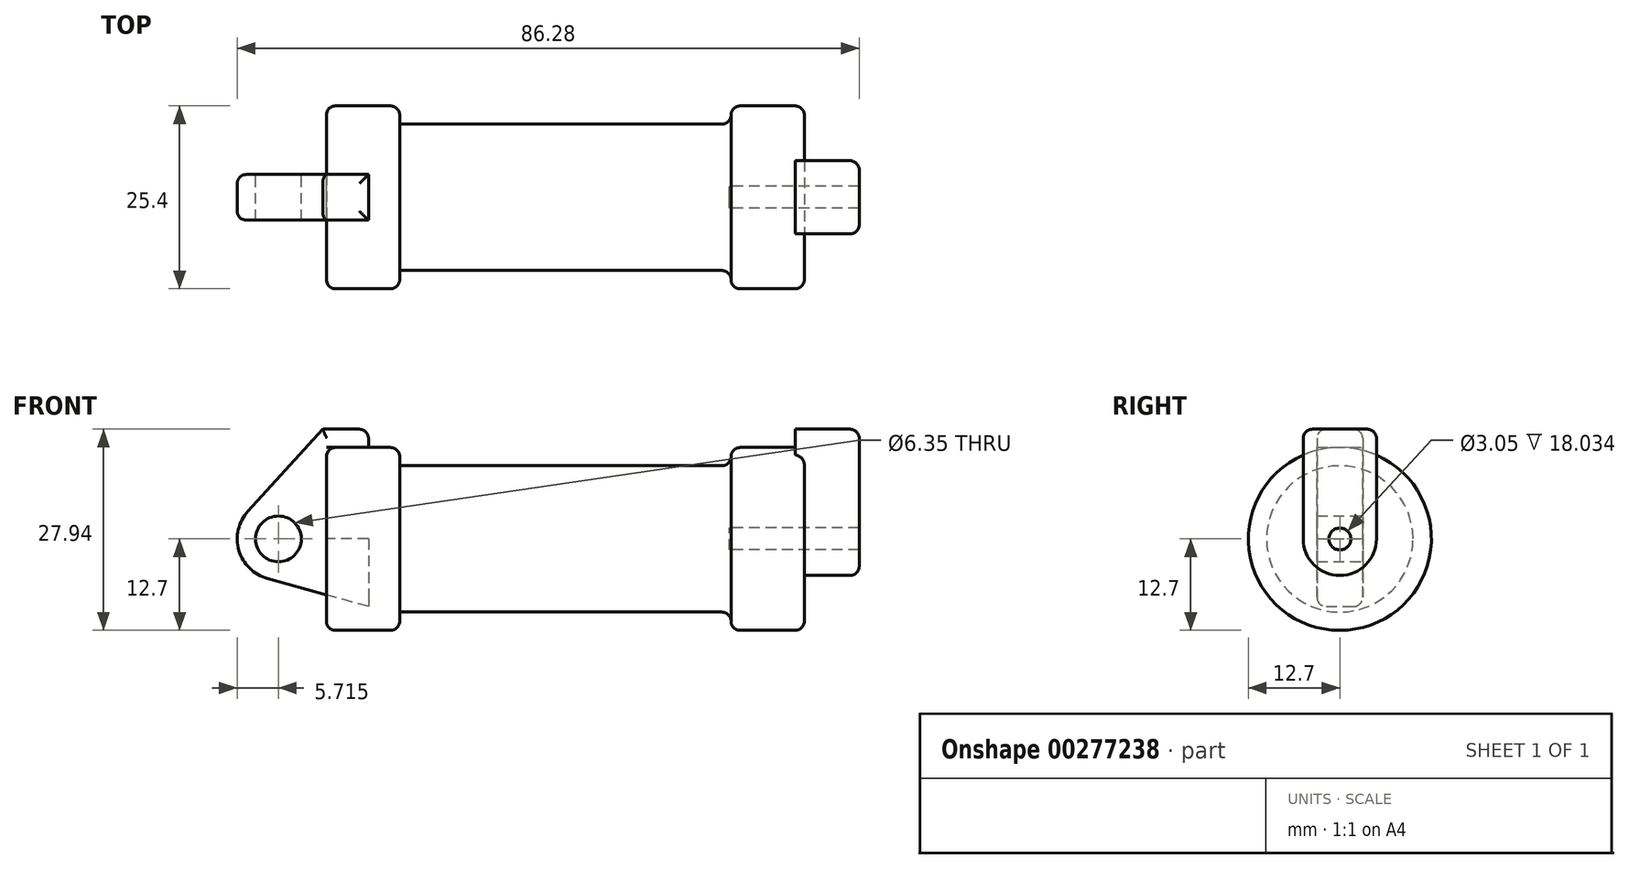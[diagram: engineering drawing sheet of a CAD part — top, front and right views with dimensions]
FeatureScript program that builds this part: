
annotation { "Feature Type Name" : "Feature", "Feature Type Description" : "" }
export const myFeature = defineFeature(function(context is Context, id is Id, definition is map)
    precondition{}
    {
        {
            var Q0;
            Q0=qCreatedBy(makeId("Front.planeOp"),FACE);
            var sketch = newSketch(context, id + "F0", { "sketchPlane" : qUnion([Q0])});
            skLineSegment(sketch, "E0", {"start": v(0, 0) * mm, "end": v(0, 12.7) * mm});
            skLineSegment(sketch, "E1", {"start": v(0, 12.7) * mm, "end": v(10.16, 12.7) * mm});
            skLineSegment(sketch, "E2", {"start": v(10.16, 12.7) * mm, "end": v(10.16, 10.16) * mm});
            skLineSegment(sketch, "E3", {"start": v(10.16, 10.16) * mm, "end": v(56.13, 10.16) * mm});
            skLineSegment(sketch, "E4", {"start": v(56.13, 10.16) * mm, "end": v(56.13, 12.7) * mm});
            skLineSegment(sketch, "E5", {"start": v(56.13, 12.7) * mm, "end": v(66.3, 12.7) * mm});
            skLineSegment(sketch, "E6", {"start": v(66.3, 12.7) * mm, "end": v(66.3, 0) * mm});
            skLineSegment(sketch, "E7", {"start": v(66.3, 0) * mm, "end": v(0, 0) * mm});
            skLineSegment(sketch, "E8", {"start": v(5.84, 15.24) * mm, "end": v(-0.5, 15.24) * mm});
            skLineSegment(sketch, "E9", {"start": v(-0.5, 15.24) * mm, "end": v(-10.88, 3.85) * mm});
            skLineSegment(sketch, "E10", {"start": v(0, 0) * mm, "end": v(-6.65, 0) * mm});
            skCircle(sketch, "E11", {"center": v(-6.65, 0) * mm, "radius": 5.72 * mm});
            skCircle(sketch, "E12", {"center": v(-6.65, 0) * mm, "radius": 3.18 * mm});
            skLineSegment(sketch, "E13", {"start": v(5.84, 15.24) * mm, "end": v(5.84, -9.4) * mm});
            skLineSegment(sketch, "E14", {"start": v(5.84, -9.4) * mm, "end": v(-8.18, -5.5) * mm});
            skSolve(sketch);
        }
        {
            var Q0;
            {var subQ0=sQuery(id+"F0.wireOp",EDGE,"E2");Q0=makeQuery(id+"F0.imprint","IMPRINT",FACE,{"disambiguationData":[TD([[makeQuery(id+"F0.imprint","IMPRINT",EDGE,{"derivedFrom":subQ0}),-1.0]])]});}
            var Q1;
            {var subQ0=sQuery(id+"F0.wireOp",EDGE,"E0");Q1=makeQuery(id+"F0.imprint","IMPRINT",FACE,{"disambiguationData":[TD([[makeQuery(id+"F0.imprint","IMPRINT",EDGE,{"derivedFrom":subQ0}),-1.0]])]});}
            var Q2;
            Q2=sQuery(id+"F0.wireOp",EDGE,"E7");
            revolve(context, id + "F1", {"entities" : qUnion([Q0, Q1]), "axis" : qUnion([Q2]), "revolveType" : RevolveType.FULL});
        }
        {
            var Q0;
            {var subQ4=sQuery(id+"F0.wireOp",EDGE,"E12");Q0=makeQuery(id+"F0.imprint","IMPRINT",FACE,{"disambiguationData":[TD([[makeQuery(id+"F0.imprint","IMPRINT",EDGE,{"derivedFrom":subQ4}),-1.0]])]});}
            var Q1;
            {var subQ0=sQuery(id+"F0.wireOp",EDGE,"E14");Q1=makeQuery(id+"F0.imprint","IMPRINT",FACE,{"disambiguationData":[TD([[makeQuery(id+"F0.imprint","IMPRINT",EDGE,{"derivedFrom":subQ0}),-1.0]])]});}
            var Q2;
            {var subQ3=sQuery(id+"F0.wireOp",EDGE,"E0");Q2=makeQuery(id+"F0.imprint","IMPRINT",FACE,{"disambiguationData":[TD([[makeQuery(id+"F0.imprint","IMPRINT",EDGE,{"derivedFrom":subQ3}),1.0]])]});}
            extrude(context, id + "F2", {"entities" : qUnion([Q0, Q1, Q2]), "depth" : 3.17 * mm, "hasSecondDirection" : true, "secondDirectionOppositeDirection" : true, "secondDirectionDepth" : 3.17 * mm});
        }
        {
            var Q0;
            Q0=makeQuery(id+"F1.opRevolve","SWEPT_FACE",FACE,{"disambiguationData":[OSD([sQuery(id+"F0.wireOp",EDGE,"E6")])]});
            var sketch = newSketch(context, id + "F3", { "sketchPlane" : qUnion([Q0])});
            skCircle(sketch, "E15", {"center": v(0, 0) * mm, "radius": 1.52 * mm});
            skCircle(sketch, "E16", {"center": v(0, 0) * mm, "radius": 5.08 * mm});
            skLineSegment(sketch, "E17", {"start": v(-5.08, 0) * mm, "end": v(-5.08, 15.24) * mm});
            skLineSegment(sketch, "E18", {"start": v(5.08, 0) * mm, "end": v(5.08, 15.24) * mm});
            skLineSegment(sketch, "E19", {"start": v(-5.08, 15.24) * mm, "end": v(5.08, 15.24) * mm});
            skSolve(sketch);
        }
        {
            var Q0;
            Q0=makeQuery(id+"F3.imprint","IMPRINT",FACE,{"disambiguationData":[TD([[makeQuery(id+"F3.imprint","IMPRINT",EDGE,{"derivedFrom":sQuery(id+"F3.wireOp",EDGE,"E15")}),-1.0]])]});
            var Q1;
            {var subQ0=sQuery(id+"F3.wireOp",EDGE,"E17");var subQ1=sQuery(id+"F3.wireOp",EDGE,"E16");var subQ2=makeQuery(id+"F3.imprint","INTERSECT",VERTEX,{"derivedFrom":[subQ1,subQ0]});Q1=makeQuery(id+"F3.imprint","IMPRINT",FACE,{"disambiguationData":[TD([[makeQuery(id+"F3.imprint","IMPRINT",EDGE,{"disambiguationData":[TD([[subQ2,1.0]])],"derivedFrom":subQ1}),-1.0]])]});}
            var Q2;
            {var subQ0=sQuery(id+"F3.wireOp",EDGE,"E19");Q2=makeQuery(id+"F3.imprint","IMPRINT",FACE,{"disambiguationData":[TD([[makeQuery(id+"F3.imprint","IMPRINT",EDGE,{"derivedFrom":subQ0}),-1.0]])]});}
            extrude(context, id + "F4", {"entities" : qUnion([Q0, Q1, Q2]), "operationType" : NewBodyOperationType.ADD, "depth" : 7.62 * mm});
        }
        {
            var Q0;
            Q0=makeQuery(id+"F4.boolean.opBoolean","SPLIT",FACE,{"disambiguationData":[TD([makeQuery(id+"F4.opExtrude","SWEPT_FACE",FACE,{"disambiguationData":[OSD([sQuery(id+"F3.wireOp",EDGE,"E15")])]})])],"derivedFrom":makeQuery(id+"F1.opRevolve","SWEPT_FACE",FACE,{"disambiguationData":[OSD([sQuery(id+"F0.wireOp",EDGE,"E6")])]})});
            extrude(context, id + "F5", {"entities" : qUnion([Q0]), "operationType" : NewBodyOperationType.REMOVE, "oppositeDirection" : true, "depth" : 10.4 * mm});
        }
        {
            var Q0;
            Q0=makeQuery(id+"F4.opExtrude","CAP_FACE",FACE,{"disambiguationData":[OSD([sQuery(id+"F3.wireOp",EDGE,"E15"),sQuery(id+"F3.wireOp",EDGE,"E16"),sQuery(id+"F3.wireOp",EDGE,"E17"),sQuery(id+"F3.wireOp",EDGE,"E18"),sQuery(id+"F3.wireOp",EDGE,"E19")])],"isStart":true});
            extrude(context, id + "F6", {"entities" : qUnion([Q0]), "operationType" : NewBodyOperationType.ADD, "depth" : 1.27 * mm});
        }
        {
            var Q0;
            Q0=makeQuery(id+"F1.opRevolve","SWEPT_EDGE",EDGE,{"disambiguationData":[OSD([sQuery(id+"F0.wireOp",EDGE,"E1"),sQuery(id+"F0.wireOp",EDGE,"E2")])]});
            var Q1;
            {var subQ0=sQuery(id+"F0.wireOp",EDGE,"E5");var subQ1=sQuery(id+"F0.wireOp",EDGE,"E6");Q1=makeQuery(id+"F4.boolean.opBoolean","SPLIT",EDGE,{"disambiguationData":[topologyDisambiguationEdgeConnected([makeQuery(id+"F1.opRevolve","SWEPT_FACE",FACE,{"disambiguationData":[OSD([subQ1])]})])],"derivedFrom":makeQuery(id+"F1.opRevolve","SWEPT_EDGE",EDGE,{"disambiguationData":[OSD([subQ0,subQ1])]})});}
            var Q2;
            {var subQ0=sQuery(id+"F3.wireOp",EDGE,"E17");Q2=makeQuery(id+"F4.boolean.opBoolean","SPLIT",EDGE,{"disambiguationData":[topologyDisambiguationEdgeConnected([makeQuery(id+"F1.opRevolve","SWEPT_FACE",FACE,{"disambiguationData":[OSD([sQuery(id+"F0.wireOp",EDGE,"E6")])]})])],"derivedFrom":makeQuery(id+"F4.opExtrude","CAP_EDGE",EDGE,{"disambiguationData":[OSD([subQ0])],"isStart":true})});}
            var Q3;
            Q3=makeQuery(id+"F1.opRevolve","SWEPT_FACE",FACE,{"disambiguationData":[OSD([sQuery(id+"F0.wireOp",EDGE,"E4")])]});
            var Q4;
            Q4=makeQuery(id+"F1.opRevolve","SWEPT_FACE",FACE,{"disambiguationData":[OSD([sQuery(id+"F0.wireOp",EDGE,"E0")])]});
            var Q5;
            Q5=makeQuery(id+"F2.opExtrude","CAP_EDGE",EDGE,{"disambiguationData":[OSD([sQuery(id+"F0.wireOp",EDGE,"E11")])],"isStart":true});
            var Q6;
            Q6=makeQuery(id+"F2.opExtrude","CAP_EDGE",EDGE,{"disambiguationData":[OSD([sQuery(id+"F0.wireOp",EDGE,"E9")])],"isStart":false});
            var Q7;
            Q7=makeQuery(id+"F2.opExtrude","CAP_EDGE",EDGE,{"disambiguationData":[OSD([sQuery(id+"F0.wireOp",EDGE,"E8")])],"isStart":false});
            var Q8;
            Q8=makeQuery(id+"F2.opExtrude","SWEPT_EDGE",EDGE,{"disambiguationData":[OSD([sQuery(id+"F0.wireOp",EDGE,"E8"),sQuery(id+"F0.wireOp",EDGE,"E13")])]});
            var Q9;
            Q9=makeQuery(id+"F2.opExtrude","CAP_EDGE",EDGE,{"disambiguationData":[OSD([sQuery(id+"F0.wireOp",EDGE,"E8")])],"isStart":true});
            var Q10;
            {var subQ0=sQuery(id+"F3.wireOp",EDGE,"E19");var subQ1=sQuery(id+"F3.wireOp",EDGE,"E17");Q10=makeQuery(id+"F6.boolean.opBoolean","MERGE",EDGE,{"derivedFrom":[makeQuery(id+"F4.opExtrude","SWEPT_EDGE",EDGE,{"disambiguationData":[OSD([subQ1,subQ0])]}),makeQuery(id+"F6.opExtrude","SWEPT_EDGE",EDGE,{"disambiguationData":[OSD([subQ1,subQ0])]})]});}
            var Q11;
            {var subQ0=sQuery(id+"F3.wireOp",EDGE,"E19");var subQ1=sQuery(id+"F3.wireOp",EDGE,"E18");Q11=makeQuery(id+"F6.boolean.opBoolean","MERGE",EDGE,{"derivedFrom":[makeQuery(id+"F4.opExtrude","SWEPT_EDGE",EDGE,{"disambiguationData":[OSD([subQ1,subQ0])]}),makeQuery(id+"F6.opExtrude","SWEPT_EDGE",EDGE,{"disambiguationData":[OSD([subQ1,subQ0])]})]});}
            var Q12;
            Q12=makeQuery(id+"F4.opExtrude","CAP_EDGE",EDGE,{"disambiguationData":[OSD([sQuery(id+"F3.wireOp",EDGE,"E17")])],"isStart":false});
            var Q13;
            Q13=makeQuery(id+"F4.opExtrude","CAP_EDGE",EDGE,{"disambiguationData":[OSD([sQuery(id+"F3.wireOp",EDGE,"E19")])],"isStart":false});
            fillet(context, id + "F7", {"entities" : qUnion([Q0, Q1, Q2, Q3, Q4, Q5, Q6, Q7, Q8, Q9, Q10, Q11, Q12, Q13]), "radius" : 1.27 * mm, "tangentPropagation" : true, "allowEdgeOverflow" : false});
        }
    });
